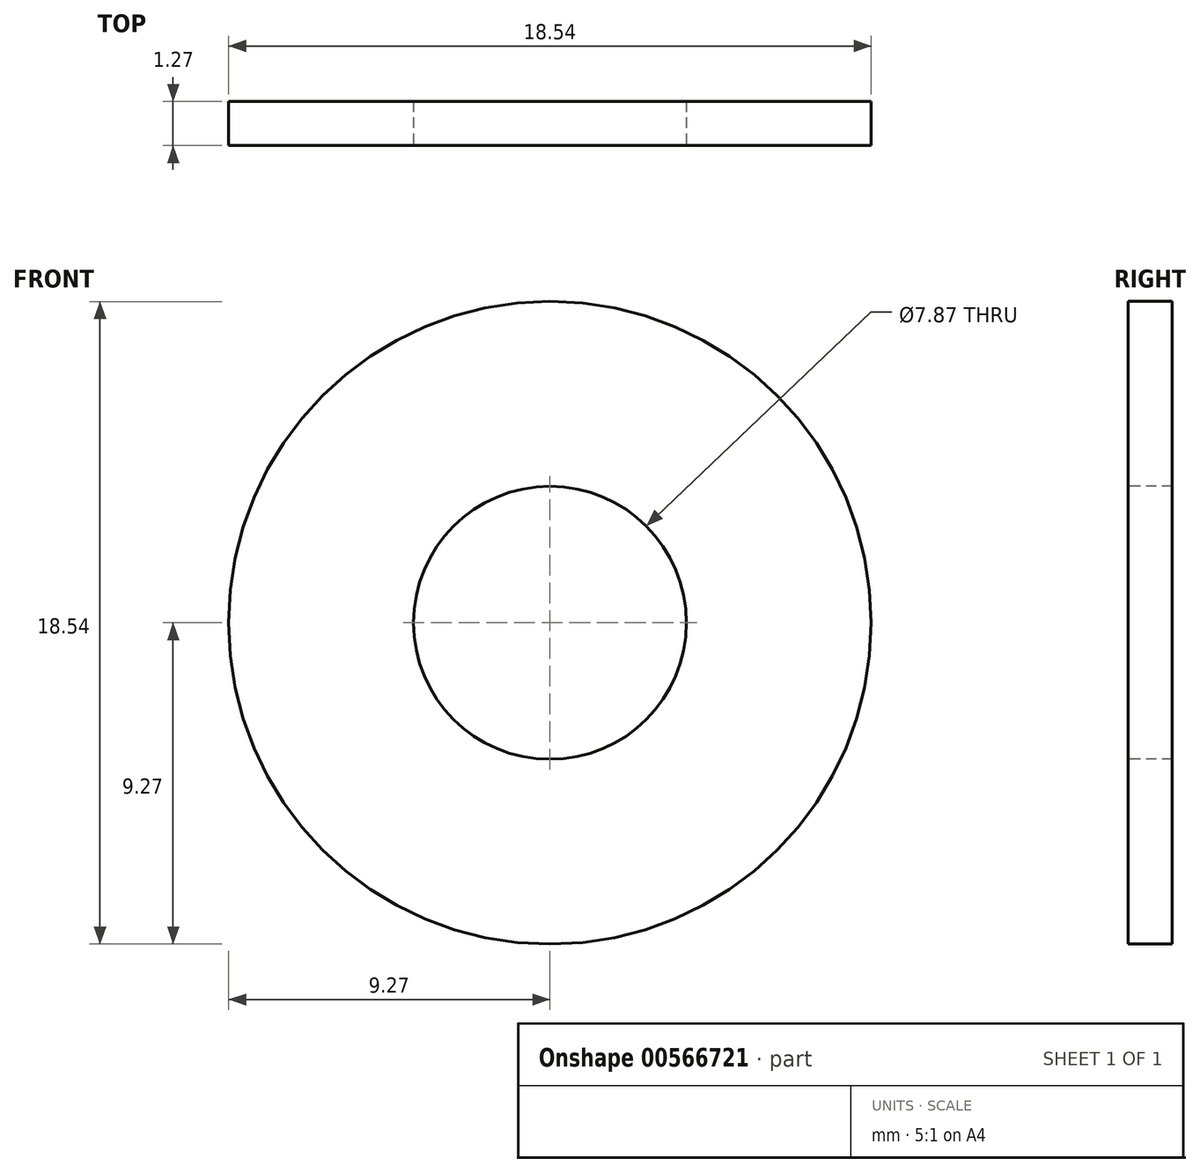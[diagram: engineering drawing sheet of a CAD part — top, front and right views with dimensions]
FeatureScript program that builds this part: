
annotation { "Feature Type Name" : "Feature", "Feature Type Description" : "" }
export const myFeature = defineFeature(function(context is Context, id is Id, definition is map)
    precondition{}
    {
        {
            var Q0;
            Q0=qCreatedBy(makeId("Front.planeOp"),FACE);
            var sketch = newSketch(context, id + "F0", { "sketchPlane" : qUnion([Q0])});
            skCircle(sketch, "E0", {"center": v(0, 0) * mm, "radius": 9.27 * mm});
            skSolve(sketch);
        }
        {
            var Q0;
            Q0=qCreatedBy(makeId("Front.planeOp"),FACE);
            var sketch = newSketch(context, id + "F1", { "sketchPlane" : qUnion([Q0])});
            skCircle(sketch, "E1", {"center": v(0, 0) * mm, "radius": 3.94 * mm});
            skSolve(sketch);
        }
        {
            var Q0;
            Q0 = qSketchRegion(id + "F0", true);
            extrude(context, id + "F2", {"entities" : qUnion([Q0]), "depth" : 1.27 * mm, "offsetDistance" : 25.4 * mm});
        }
        {
            var Q0;
            Q0 = qSketchRegion(id + "F1", true);
            extrude(context, id + "F3", {"entities" : qUnion([Q0]), "operationType" : NewBodyOperationType.REMOVE, "endBound" : BoundingType.SYMMETRIC, "oppositeDirection" : true, "depth" : 25.4 * mm, "offsetDistance" : 25.4 * mm});
        }
    });
